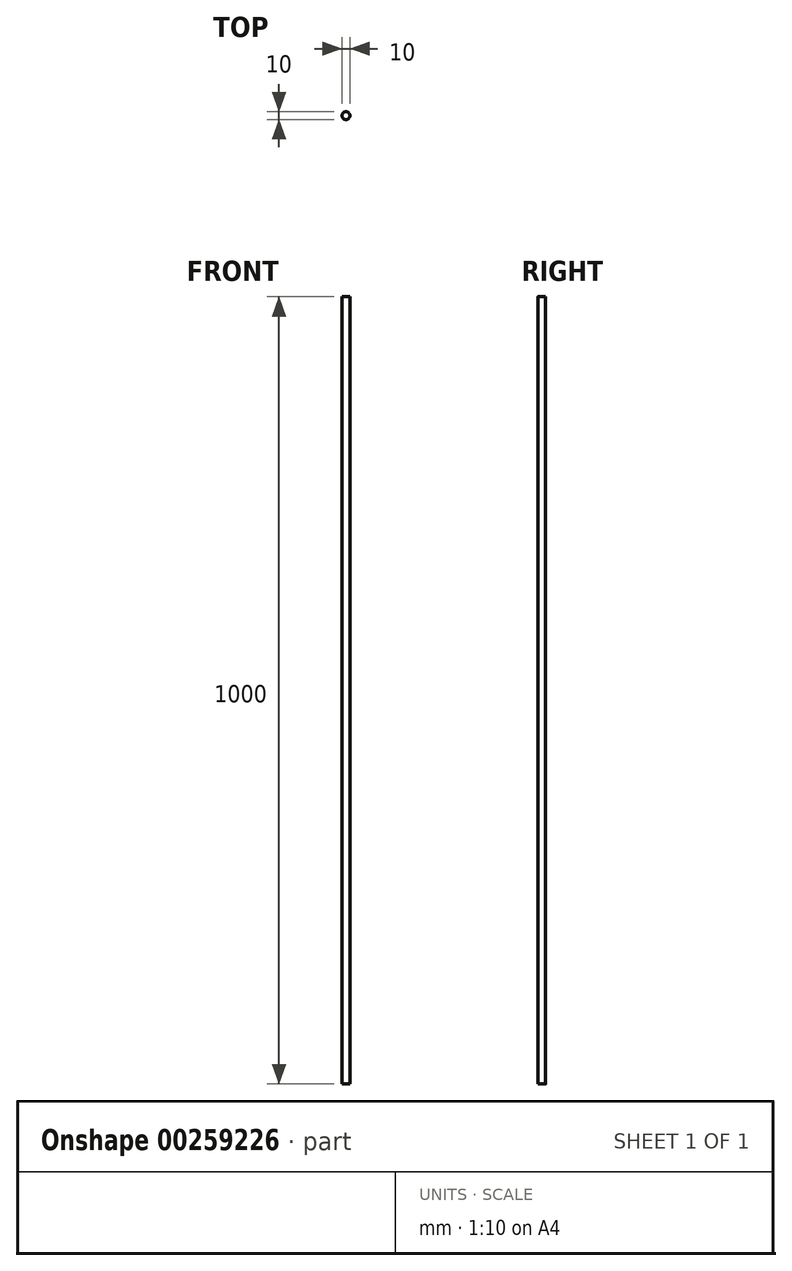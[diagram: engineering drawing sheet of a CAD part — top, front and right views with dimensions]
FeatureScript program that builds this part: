
annotation { "Feature Type Name" : "Feature", "Feature Type Description" : "" }
export const myFeature = defineFeature(function(context is Context, id is Id, definition is map)
    precondition{}
    {
        {
            var Q0;
            Q0=qCreatedBy(makeId("Top.planeOp"),FACE);
            var sketch = newSketch(context, id + "F0", { "sketchPlane" : qUnion([Q0])});
            skCircle(sketch, "E0", {"center": v(0, 0) * mm, "radius": 5 * mm});
            skSolve(sketch);
        }
        {
            var Q0;
            Q0=qSketchRegion(id+"F0",true);
            extrude(context, id + "F1", {"entities" : qUnion([Q0]), "depth" : 1000 * mm});
        }
    });
